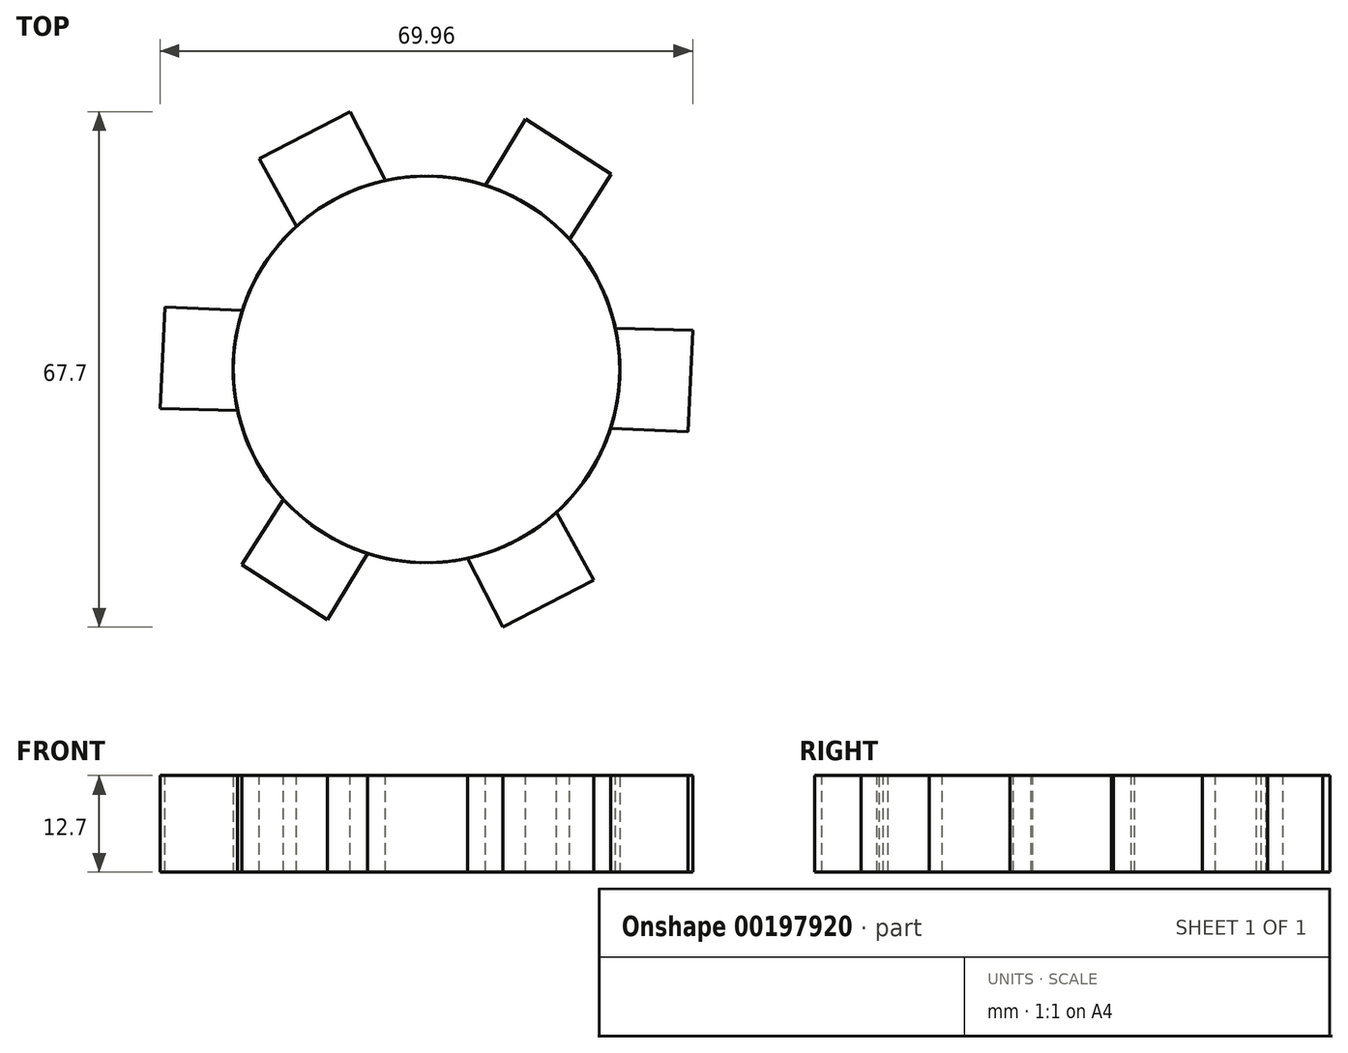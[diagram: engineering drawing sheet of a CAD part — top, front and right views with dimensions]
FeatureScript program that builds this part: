
annotation { "Feature Type Name" : "Feature", "Feature Type Description" : "" }
export const myFeature = defineFeature(function(context is Context, id is Id, definition is map)
    precondition{}
    {
        {
            var Q0;
            Q0=qCreatedBy(makeId("Top.planeOp"),FACE);
            var sketch = newSketch(context, id + "F0", { "sketchPlane" : qUnion([Q0])});
            skCircle(sketch, "E0", {"center": v(0, 0) * mm, "radius": 25.4 * mm});
            skSolve(sketch);
        }
        {
            var Q0;
            Q0 = qSketchRegion(id + "F0", true);
            extrude(context, id + "F1", {"entities" : qUnion([Q0]), "endBound" : BoundingType.SYMMETRIC, "depth" : 12.7 * mm});
        }
        {
            var Q0;
            Q0=makeQuery(id+"F1.opExtrude","CAP_FACE",FACE,{"disambiguationData":[OSD([sQuery(id+"F0.wireOp",EDGE,"E0")])],"isStart":false});
            var sketch = newSketch(context, id + "F2", { "sketchPlane" : qUnion([Q0])});
            skLineSegment(sketch, "E1", {"start": v(0, 0) * mm, "end": v(-25.37, 1.2) * mm});
            skLineSegment(sketch, "E2", {"start": v(0, 0) * mm, "end": v(-24.2, 7.73) * mm});
            skLineSegment(sketch, "E3", {"start": v(0, 0) * mm, "end": v(-24.82, -5.4) * mm});
            skLineSegment(sketch, "E4", {"start": v(-24.82, -5.4) * mm, "end": v(-24.2, 7.73) * mm});
            skLineSegment(sketch, "E5.0", {"start": v(-34.98, -5.16) * mm, "end": v(-34.34, 8.2) * mm});
            skLineSegment(sketch, "E6", {"start": v(-34.98, -5.16) * mm, "end": v(-24.82, -5.4) * mm});
            skLineSegment(sketch, "E7", {"start": v(-34.34, 8.2) * mm, "end": v(-24.2, 7.73) * mm});
            skSolve(sketch);
        }
        {
            var Q0;
            Q0 = qSketchRegion(id + "F2", true);
            extrude(context, id + "F3", {"entities" : qUnion([Q0]), "operationType" : NewBodyOperationType.ADD, "oppositeDirection" : true, "depth" : 12.7 * mm});
        }
        {
            var Q0;
            Q0=qCreatedBy(makeId("Right.planeOp"),FACE);
            var sketch = newSketch(context, id + "F4", { "sketchPlane" : qUnion([Q0])});
            skLineSegment(sketch, "E8", {"start": v(0, 0) * mm, "end": v(0, 35.92) * mm});
            skSolve(sketch);
        }
        {
            var Q0;
            Q0=makeQuery(id+"F1.opExtrude","SWEPT_BODY",BODY,{"disambiguationData":[OSD([sQuery(id+"F0.wireOp",EDGE,"E0")])]});
            var Q1;
            Q1=sQuery(id+"F4.wireOp",EDGE,"E8");
            circularPattern(context, id + "F5", {"entities" : qUnion([Q0]), "axis" : qUnion([Q1]), "angle" : 360 * degree, "instanceCount" : 6, "equalSpace" : true});
        }
    });
